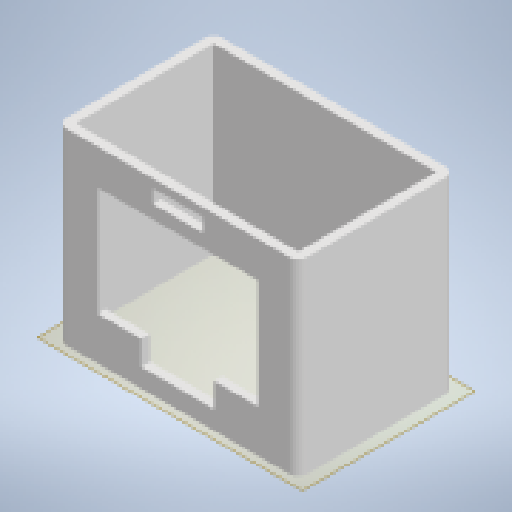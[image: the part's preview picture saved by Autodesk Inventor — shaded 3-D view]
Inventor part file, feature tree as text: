
AUTODESK INVENTOR PART (.ipt)
format: ipt  version: 2024 (Build 280153000, 153)  size: 512,512 bytes
history: native  units: mm
features: sketch x20, extrude x19, projected_geometry x18, reference x10, other x6, plane x2, fillet x1
ambient origin geometry x8: Origin, YZ Plane, XZ Plane, XY Plane, X Axis, Y Axis, Z Axis, Center Point
bodies: Volumenkörper1 (feature_tree)
feature tree (76):
  plane  "Arbeitsebene1"
  extrude  "Extrusion1"  Depth=2.2mm TaperAngle=0.0deg
  extrude  "Extrusion2"  Depth=38.0mm
  extrude  "Extrusion3"  Depth=2.0mm
  extrude  "Extrusion4"  Depth=7.82mm
  extrude  "Extrusion5"  Depth=0.2mm
  extrude  "Extrusion6"  Depth=0.2mm
  extrude  "Extrusion7"  Depth=0.3mm
  extrude  "Extrusion8"  Depth=1.8mm
  extrude  "Extrusion9"  Depth=10.0mm TaperAngle=0.0deg
  extrude  "Extrusion10"  Depth=8.0mm
  extrude  "Extrusion11"  Depth=8.0mm
  fillet  "Rundung1"  Radius=5.5mm
  plane  "Arbeitsebene2"
  extrude  "Extrusion12"  Depth=2.0mm
  extrude  "Extrusion13"  Depth=10.0mm TaperAngle=0.0deg
  extrude  "Extrusion14"  Depth=2.0mm
  extrude  "Extrusion15"  Depth=10.0mm TaperAngle=0.0deg
  extrude  "Extrusion16"  Depth=2.0mm TaperAngle=0.0deg
  extrude  "Extrusion17"  Depth=2.0mm TaperAngle=0.0deg
  extrude  "Extrusion18"  Depth=2.0mm TaperAngle=0.0deg
  sketch  "Skizze21"  dims[d57=2.0mm d58=2.0mm d59=0.0mm]
  extrude  "Extrusion19"  Depth=2.0mm TaperAngle=0.0deg
  sketch  "Skizze1"  dims[d0=0.2mm d1=2.2mm d2=0.0mm]
  reference  "Referenz1"
  sketch  "Skizze2"  dims[d3=38.0mm d4=0.0mm d5=36.0mm]
  reference  "Referenz2"
  reference  "Referenz3"
  projected_geometry  "Projizierte Kontur1"
  sketch  "Skizze3"  dims[d6=34.0mm d7=2.0mm]
  reference  "Referenz4"
  sketch  "Skizze4"  dims[d8=7.82mm d9=7.82mm]
  projected_geometry  "Projizierte Kontur2"
  sketch  "Skizze5"  dims[d10=38.0mm d11=0.0mm d12=0.2mm]
  projected_geometry  "Projizierte Kontur3"
  reference  "Referenz5"
  sketch  "Skizze6"  dims[d13=10.0mm d14=0.0mm d15=0.2mm]
  reference  "Referenz6"
  sketch  "Skizze7"  dims[d16=0.5mm d17=0.3mm]
  projected_geometry  "Projizierte Kontur4"
  sketch  "Skizze8"  dims[d18=1.8mm d19=0.0mm d20=1.6mm]
  reference  "Referenz7"
  reference  "Referenz8"
  sketch  "Skizze9"  dims[d21=1.8mm d22=0.0mm d23=10.0mm d24=0.0mm]
  projected_geometry  "Projizierte Kontur5"
  projected_geometry  "Projizierte Kontur6"
  sketch  "Skizze10"  dims[d25=2.5mm d26=8.0mm]
  sketch  "Skizze11"  dims[d27=2.5mm d28=8.0mm d29=5.5mm d30=0.0mm]
  projected_geometry  "Projizierte Kontur7"
  projected_geometry  "Projizierte Kontur8"
  sketch  "Skizze12"  dims[d31=3.5mm d32=2.0mm]
  reference  "Referenz9"
  sketch  "Skizze13"  dims[d33=5.5mm d34=0.0mm d35=10.0mm d36=0.0mm]
  projected_geometry  "Projizierte Kontur9"
  projected_geometry  "Projizierte Kontur10"
  projected_geometry  "Projizierte Kontur11"
  projected_geometry  "Projizierte Kontur12"
  reference  "Referenz10"
  sketch  "Skizze15"  dims[d37=1.0mm d38=0.0mm d39=2.0mm]
  projected_geometry  "Projizierte Kontur14"
  sketch  "Skizze17"  dims[d40=1.0mm d41=0.0mm d42=10.0mm d43=0.0mm]
  projected_geometry  "Projizierte Kontur16"
  sketch  "Skizze18"  dims[d46=2.0mm d47=0.0mm d49=2.0mm d50=0.0mm]
  projected_geometry  "Projizierte Kontur17"
  sketch  "Skizze19"  dims[d51=2.0mm d52=2.0mm d53=0.0mm]
  projected_geometry  "Projizierte Kontur18"
  sketch  "Skizze20"  dims[d54=6.5mm d55=2.0mm d56=0.0mm]
  sketch  "Skizze22"  dims[d60=1.0mm d61=0.0mm]
  projected_geometry  "Projizierte Kontur19"
  projected_geometry  "Projizierte Kontur20"
  parser-record x1  (decoder bookkeeping rows leaked as tree rows — omitted from the tree; the rows remain in map.json)
  other  "main.iam"
  other  "Gehaeuse_unten:1"
  other  "Oled SH1106:1"
  other  "ESP32-C3 supermini v5:2"
  other  "GY-BME280:1"
note: 1 file-system path scrubbed to <path> (originals preserved in map.json)
